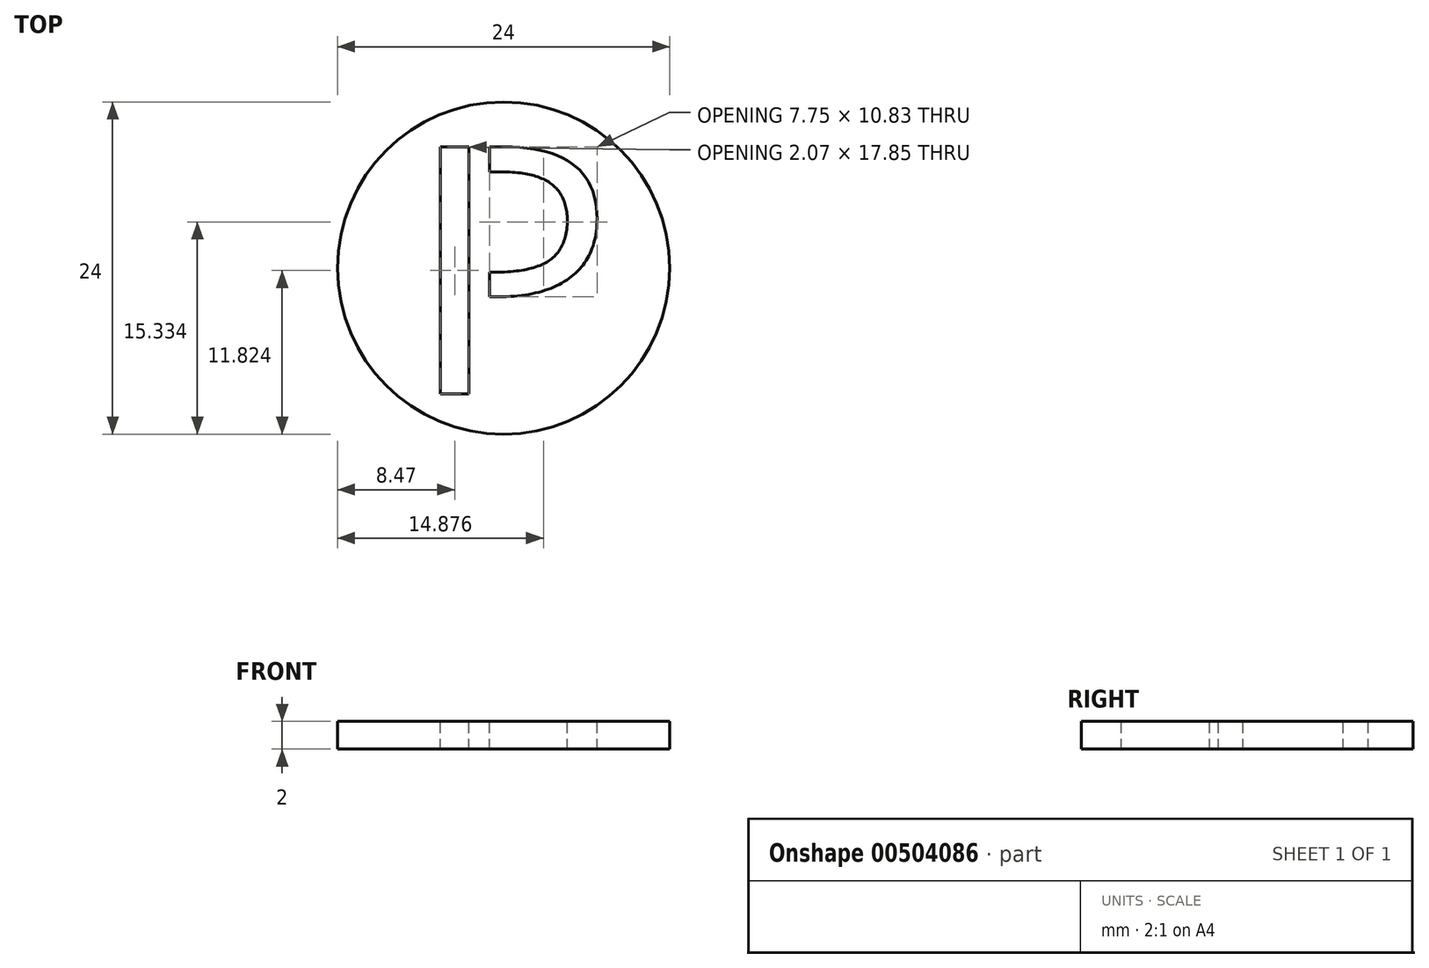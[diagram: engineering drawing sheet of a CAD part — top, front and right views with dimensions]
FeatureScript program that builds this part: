
annotation { "Feature Type Name" : "Feature", "Feature Type Description" : "" }
export const myFeature = defineFeature(function(context is Context, id is Id, definition is map)
    precondition{}
    {
        {
            var Q0;
            Q0=qCreatedBy(makeId("Top.planeOp"),FACE);
            var sketch = newSketch(context, id + "F0", { "sketchPlane" : qUnion([Q0])});
            skCircle(sketch, "E0", {"center": v(0, 0) * mm, "radius": 12 * mm});
            skSolve(sketch);
        }
        {
            var Q0;
            Q0=qSketchRegion(id+"F0",true);
            extrude(context, id + "F1", {"entities" : qUnion([Q0]), "depth" : 2 * mm});
        }
        {
            var Q0;
            Q0=makeQuery(id+"F1.opExtrude","CAP_FACE",FACE,{"disambiguationData":[OSD([sQuery(id+"F0.wireOp",EDGE,"E0")])],"isStart":false});
            var sketch = newSketch(context, id + "F2", { "sketchPlane" : qUnion([Q0])});
            skText(sketch, "E1", { "text": "P", "fontName": "OpenSans-Regular.ttf"});
            skLineSegment(sketch, "E2.bottom", {"start": v(-2.5, -2.73) * mm, "end": v(-1, -2.73) * mm});
            skLineSegment(sketch, "E2.top", {"start": v(-2.5, 8.9) * mm, "end": v(-1, 8.9) * mm});
            skLineSegment(sketch, "E2.left", {"start": v(-2.5, -2.73) * mm, "end": v(-2.5, 8.9) * mm});
            skLineSegment(sketch, "E2.right", {"start": v(-1, -2.73) * mm, "end": v(-1, 8.9) * mm});
            const initialGuessF2  = {"E1": [-0.00702, -0.0091, 1, 0, 0.018]};
            skSetInitialGuess(sketch, initialGuessF2);
            skSolve(sketch);
        }
        {
            var Q0;
            {var subQ4=sQuery(id+"F2.wireOp",EDGE,"E1.sketch_text.stroke-4");Q0=makeQuery(id+"F2.imprint","IMPRINT",FACE,{"disambiguationData":[TD([[makeQuery(id+"F2.imprint","IMPRINT",EDGE,{"derivedFrom":subQ4}),-1.0]])]});}
            var Q1;
            Q1=makeQuery(id+"F2.imprint","IMPRINT",FACE,{"disambiguationData":[TD([[makeQuery(id+"F2.imprint","IMPRINT",EDGE,{"derivedFrom":sQuery(id+"F2.wireOp",EDGE,"E1.sketch_text.stroke-0")}),-1.0]])]});
            extrude(context, id + "F3", {"entities" : qUnion([Q0, Q1]), "operationType" : NewBodyOperationType.REMOVE, "oppositeDirection" : true, "depth" : 25 * mm, "offsetDistance" : 25 * mm});
        }
    });
